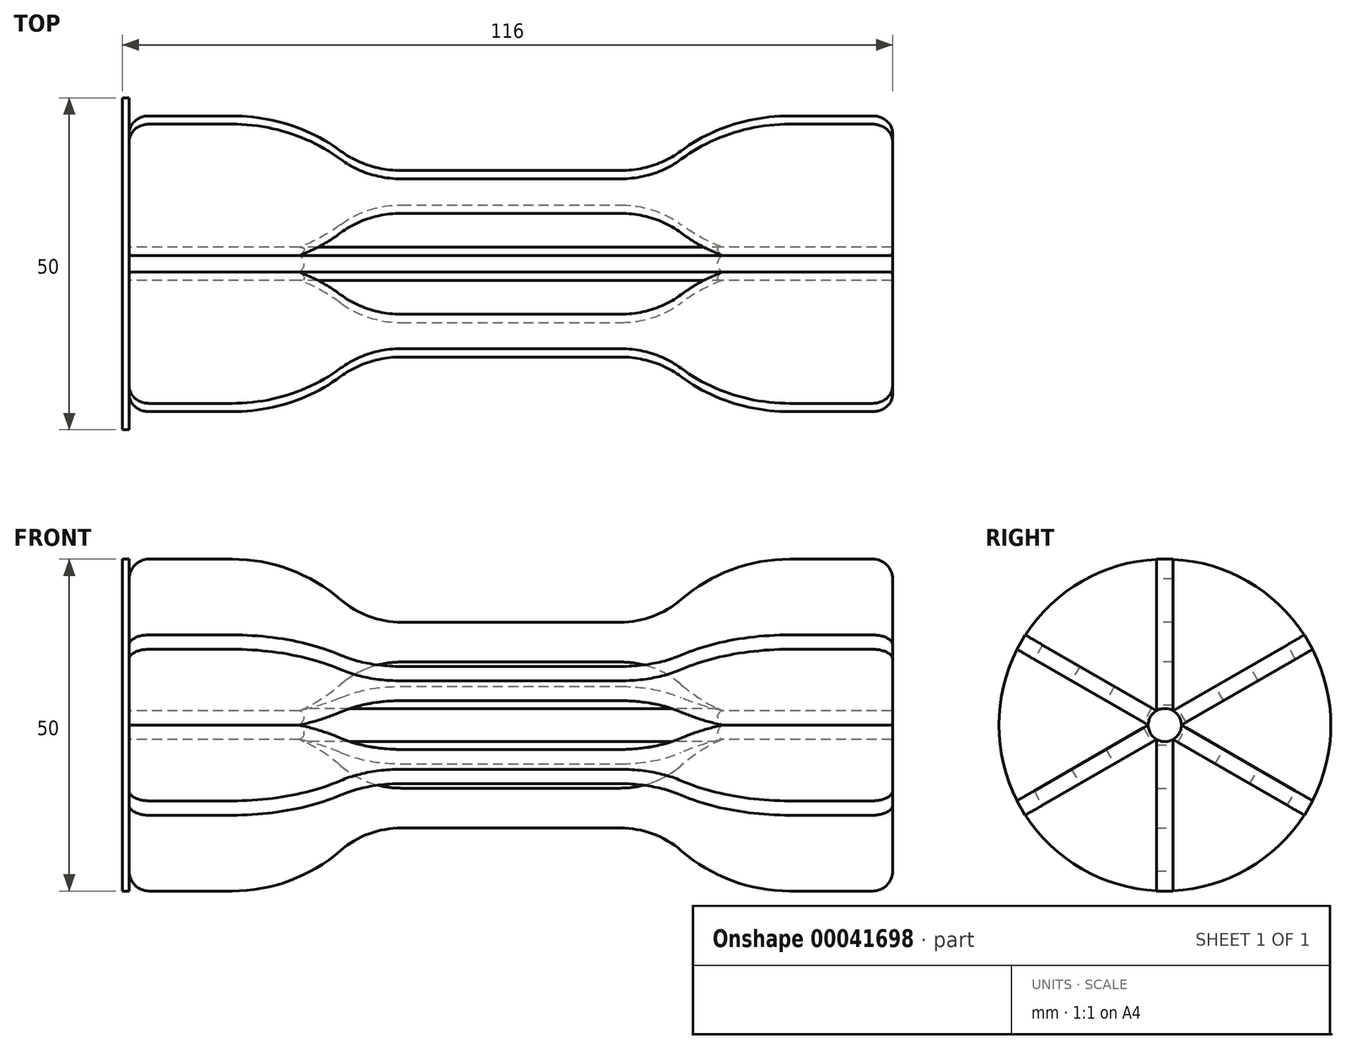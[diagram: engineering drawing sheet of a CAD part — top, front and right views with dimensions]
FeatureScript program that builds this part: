
annotation { "Feature Type Name" : "Feature", "Feature Type Description" : "" }
export const myFeature = defineFeature(function(context is Context, id is Id, definition is map)
    precondition{}
    {
        {
            var Q0;
            Q0=qCreatedBy(makeId("Front.planeOp"),FACE);
            var sketch = newSketch(context, id + "F0", { "sketchPlane" : qUnion([Q0])});
            skLineSegment(sketch, "E0", {"start": v(-54.5, 12.5) * mm, "end": v(-42, 12.5) * mm});
            skLineSegment(sketch, "E1", {"start": v(-25.66, 6.41) * mm, "end": v(-25.66, 6.41) * mm});
            skArc(sketch, "E2.filletArc", {"start": v(-25.66, 6.41) * mm, "mid": v(-21.39, 3.88) * mm, "end": v(-16.5, 3) * mm});
            skArc(sketch, "E3.filletArc", {"start": v(-25.66, 6.41) * mm, "mid": v(-33.29, 10.93) * mm, "end": v(-42, 12.5) * mm});
            skArc(sketch, "E4.MirrorCS", {"start": v(25.66, 6.41) * mm, "mid": v(21.39, 3.88) * mm, "end": v(16.5, 3) * mm});
            skLineSegment(sketch, "E5.MirrorCS", {"start": v(54.5, 12.5) * mm, "end": v(42, 12.5) * mm});
            skLineSegment(sketch, "E6.MirrorCS", {"start": v(25.66, 6.41) * mm, "end": v(25.66, 6.41) * mm});
            skArc(sketch, "E7.MirrorCS", {"start": v(25.66, 6.41) * mm, "mid": v(33.29, 10.93) * mm, "end": v(42, 12.5) * mm});
            skArc(sketch, "E8.MirrorCS", {"start": v(25.66, -6.41) * mm, "mid": v(21.39, -3.88) * mm, "end": v(16.5, -3) * mm});
            skArc(sketch, "E9.MirrorCS", {"start": v(-25.66, -6.41) * mm, "mid": v(-21.39, -3.88) * mm, "end": v(-16.5, -3) * mm});
            skLineSegment(sketch, "E10.MirrorCS", {"start": v(-25.66, -6.41) * mm, "end": v(-25.66, -6.41) * mm});
            skArc(sketch, "E11.MirrorCS", {"start": v(25.66, -6.41) * mm, "mid": v(33.29, -10.93) * mm, "end": v(42, -12.5) * mm});
            skLineSegment(sketch, "E12.MirrorCS", {"start": v(54.5, -12.5) * mm, "end": v(42, -12.5) * mm});
            skArc(sketch, "E13.MirrorCS", {"start": v(-25.66, -6.41) * mm, "mid": v(-33.29, -10.93) * mm, "end": v(-42, -12.5) * mm});
            skLineSegment(sketch, "E14.MirrorCS", {"start": v(-54.5, -12.5) * mm, "end": v(-42, -12.5) * mm});
            skLineSegment(sketch, "E15.MirrorCS", {"start": v(25.66, -6.41) * mm, "end": v(25.66, -6.41) * mm});
            skArc(sketch, "E16.filletArc", {"start": v(-54.5, 12.5) * mm, "mid": v(-56.62, 11.62) * mm, "end": v(-57.5, 9.5) * mm});
            skArc(sketch, "E17.filletArc", {"start": v(-57.5, -9.5) * mm, "mid": v(-56.62, -11.62) * mm, "end": v(-54.5, -12.5) * mm});
            skArc(sketch, "E18.filletArc", {"start": v(57.5, 9.5) * mm, "mid": v(56.62, 11.62) * mm, "end": v(54.5, 12.5) * mm});
            skArc(sketch, "E19.filletArc", {"start": v(54.5, -12.5) * mm, "mid": v(56.62, -11.62) * mm, "end": v(57.5, -9.5) * mm});
            skLineSegment(sketch, "E20", {"start": v(-57.5, 9.5) * mm, "end": v(-57.5, -9.5) * mm});
            skLineSegment(sketch, "E21", {"start": v(57.5, 9.5) * mm, "end": v(57.5, -9.5) * mm});
            skLineSegment(sketch, "E22", {"start": v(-16.5, 3) * mm, "end": v(16.5, 3) * mm});
            skLineSegment(sketch, "E23", {"start": v(-16.5, -3) * mm, "end": v(16.5, -3) * mm});
            skSolve(sketch);
        }
        {
            var Q0;
            Q0 = qSketchRegion(id + "F0", true);
            extrude(context, id + "F1", {"entities" : qUnion([Q0]), "depth" : 2.5 * mm});
        }
        {
            var Q0;
            Q0=makeQuery(id+"F1.opExtrude","SWEPT_FACE",FACE,{"disambiguationData":[OSD([sQuery(id+"F0.wireOp",EDGE,"E5.MirrorCS")])]});
            var sketch = newSketch(context, id + "F2", { "sketchPlane" : qUnion([Q0])});
            skLineSegment(sketch, "E24", {"start": v(54.5, -1.25) * mm, "end": v(-54.48, -1.25) * mm, "construction": true});
            skPoint(sketch, "E24.endSnap0", {"position": v(42, -1.25) * mm});
            skSolve(sketch);
        }
        {
            var Q0;
            Q0=makeQuery(id+"F1.opExtrude","SWEPT_BODY",BODY,{"disambiguationData":[OSD([sQuery(id+"F0.wireOp",EDGE,"E0"),sQuery(id+"F0.wireOp",EDGE,"E2.filletArc"),sQuery(id+"F0.wireOp",EDGE,"E3.filletArc"),sQuery(id+"F0.wireOp",EDGE,"E4.MirrorCS"),sQuery(id+"F0.wireOp",EDGE,"E5.MirrorCS"),sQuery(id+"F0.wireOp",EDGE,"E7.MirrorCS"),sQuery(id+"F0.wireOp",EDGE,"E8.MirrorCS"),sQuery(id+"F0.wireOp",EDGE,"E9.MirrorCS"),sQuery(id+"F0.wireOp",EDGE,"E11.MirrorCS"),sQuery(id+"F0.wireOp",EDGE,"E12.MirrorCS"),sQuery(id+"F0.wireOp",EDGE,"E13.MirrorCS"),sQuery(id+"F0.wireOp",EDGE,"E14.MirrorCS"),sQuery(id+"F0.wireOp",EDGE,"E16.filletArc"),sQuery(id+"F0.wireOp",EDGE,"E17.filletArc"),sQuery(id+"F0.wireOp",EDGE,"E18.filletArc"),sQuery(id+"F0.wireOp",EDGE,"E19.filletArc"),sQuery(id+"F0.wireOp",EDGE,"E20"),sQuery(id+"F0.wireOp",EDGE,"E21"),sQuery(id+"F0.wireOp",EDGE,"E22"),sQuery(id+"F0.wireOp",EDGE,"E23")])]});
            var Q1;
            Q1=sQuery(id+"F2.wireOp",EDGE,"E24");
            circularPattern(context, id + "F3", {"operationType" : NewBodyOperationType.ADD, "entities" : qUnion([Q0]), "axis" : qUnion([Q1]), "angle" : 360 * degree, "instanceCount" : 6, "equalSpace" : true});
        }
        {
            var Q0;
            Q0=makeQuery(id+"F1.opExtrude","SWEPT_FACE",FACE,{"disambiguationData":[OSD([sQuery(id+"F0.wireOp",EDGE,"E20")])]});
            var sketch = newSketch(context, id + "F4", { "sketchPlane" : qUnion([Q0])});
            skPoint(sketch, "E25.0", {"position": v(1.25, 12.5) * mm});
            skCircle(sketch, "E26", {"center": v(1.25, 12.5) * mm, "radius": 2.5 * mm});
            skSolve(sketch);
        }
        {
            var Q0;
            Q0=makeQuery(id+"F4.imprint","IMPRINT",FACE,{"disambiguationData":[TD([[makeQuery(id+"F4.imprint","IMPRINT",EDGE,{"derivedFrom":sQuery(id+"F4.wireOp",EDGE,"E26")}),1.0]])]});
            var Q1;
            Q1=makeQuery(id+"F3.opPattern","COPY",FACE,{"derivedFrom":makeQuery(id+"F1.opExtrude","SWEPT_FACE",FACE,{"disambiguationData":[OSD([sQuery(id+"F0.wireOp",EDGE,"E21")])]}),"instanceName":"1"});
            extrude(context, id + "F5", {"entities" : qUnion([Q0]), "operationType" : NewBodyOperationType.ADD, "endBound" : BoundingType.UP_TO_SURFACE, "oppositeDirection" : true, "endBoundEntityFace" : qUnion([Q1]), "depth" : 25 * mm});
        }
        {
            var Q0;
            Q0=makeQuery(id+"F5.opExtrude","CAP_FACE",FACE,{"disambiguationData":[OSD([sQuery(id+"F4.wireOp",EDGE,"E26")])],"isStart":true});
            var sketch = newSketch(context, id + "F6", { "sketchPlane" : qUnion([Q0])});
            skCircle(sketch, "E27", {"center": v(1.25, 12.5) * mm, "radius": 25 * mm});
            skSolve(sketch);
        }
        {
            var Q0;
            Q0 = qSketchRegion(id + "F6", true);
            extrude(context, id + "F7", {"entities" : qUnion([Q0]), "operationType" : NewBodyOperationType.ADD, "depth" : 1 * mm});
        }
    });
